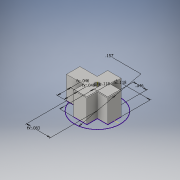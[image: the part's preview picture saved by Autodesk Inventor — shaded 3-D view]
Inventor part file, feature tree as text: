
AUTODESK INVENTOR PART (.ipt)
format: ipt  version: 2016 (Build 200138000, 138)  size: 114,176 bytes
history: native  units: in
note: dims shown in document units (in); Inventor stores cm internally (conversion verified against a paired STEP export)
features: other x1, extrude x1, hole x1
ambient origin geometry x8: Origin, YZ Plane, XZ Plane, XY Plane, X Axis, Y Axis, Z Axis, Center Point
bodies: Body1 (feature_tree)
feature tree (3):
  other  "base+body"
  extrude  "Extrusion6"  Depth=0.1575in
  hole  "Hole4"  [1 undecoded]
note: 1 required parameter value undecoded (feature->parameter linkage not recoverable at this tier; creation-order binding heuristic only, values carry confidence <= 0.55)
